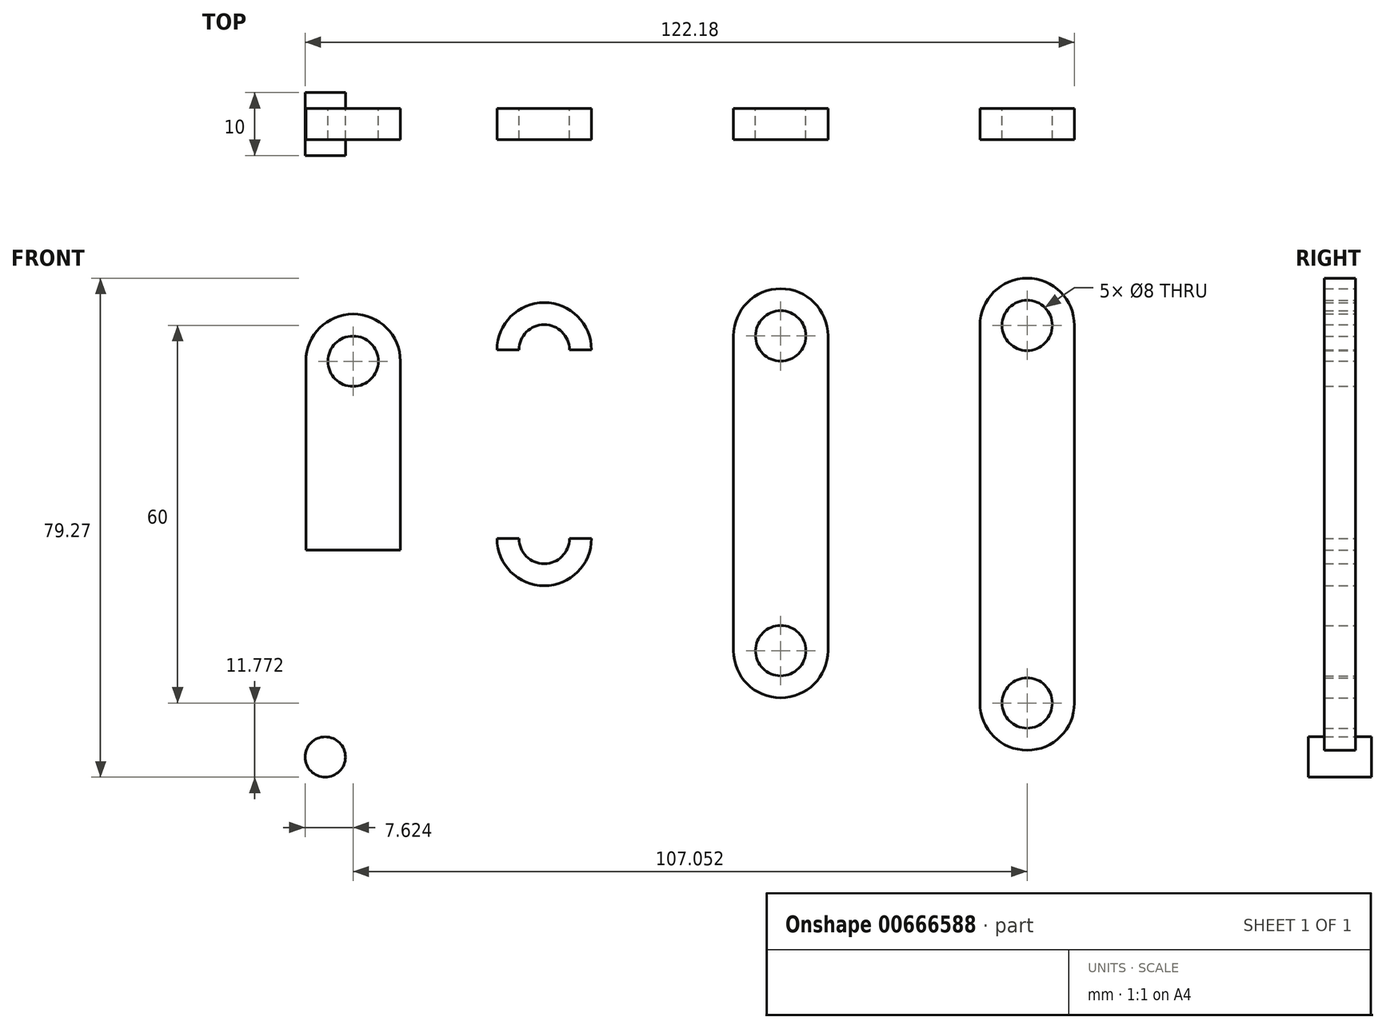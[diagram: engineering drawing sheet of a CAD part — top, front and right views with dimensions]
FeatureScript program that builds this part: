
annotation { "Feature Type Name" : "Feature", "Feature Type Description" : "" }
export const myFeature = defineFeature(function(context is Context, id is Id, definition is map)
    precondition{}
    {
        {
            var Q0;
            Q0=qCreatedBy(makeId("Front.planeOp"),FACE);
            var sketch = newSketch(context, id + "F0", { "sketchPlane" : qUnion([Q0])});
            skLineSegment(sketch, "E0.bottom", {"start": v(-59.87, 52.34) * mm, "end": v(-44.87, 52.34) * mm});
            skLineSegment(sketch, "E0.top", {"start": v(-59.87, 22.34) * mm, "end": v(-44.87, 22.34) * mm});
            skLineSegment(sketch, "E0.left", {"start": v(-59.87, 52.34) * mm, "end": v(-59.87, 22.34) * mm});
            skLineSegment(sketch, "E0.right", {"start": v(-44.87, 52.34) * mm, "end": v(-44.87, 22.34) * mm});
            skArc(sketch, "E1", {"start": v(-44.87, 52.34) * mm, "mid": v(-52.37, 59.84) * mm, "end": v(-59.87, 52.34) * mm});
            skCircle(sketch, "E2", {"center": v(-52.37, 52.34) * mm, "radius": 4 * mm});
            skSolve(sketch);
        }
        {
            var Q0;
            {var subQ0=sQuery(id+"F0.wireOp",EDGE,"E1");Q0=makeQuery(id+"F0.imprint","IMPRINT",FACE,{"disambiguationData":[TD([[makeQuery(id+"F0.imprint","IMPRINT",EDGE,{"derivedFrom":subQ0}),1.0]])]});}
            var Q1;
            Q1=makeQuery(id+"F0.imprint","IMPRINT",FACE,{"disambiguationData":[TD([[makeQuery(id+"F0.imprint","IMPRINT",EDGE,{"derivedFrom":sQuery(id+"F0.wireOp",EDGE,"E0.top")}),1.0]])]});
            extrude(context, id + "F1", {"entities" : qUnion([Q0, Q1]), "depth" : 5 * mm, "offsetDistance" : 25.4 * mm, "symmetric" : true});
        }
        {
            var Q0;
            Q0=qCreatedBy(makeId("Front.planeOp"),FACE);
            var sketch = newSketch(context, id + "F2", { "sketchPlane" : qUnion([Q0])});
            skLineSegment(sketch, "E3.bottom", {"start": v(-29.52, 54.16) * mm, "end": v(-14.52, 54.16) * mm});
            skLineSegment(sketch, "E3.top", {"start": v(-29.52, 24.16) * mm, "end": v(-14.52, 24.16) * mm});
            skLineSegment(sketch, "E3.left", {"start": v(-29.52, 54.16) * mm, "end": v(-29.52, 24.16) * mm});
            skLineSegment(sketch, "E3.right", {"start": v(-14.52, 54.16) * mm, "end": v(-14.52, 24.16) * mm});
            skArc(sketch, "E4", {"start": v(-29.52, 24.16) * mm, "mid": v(-22.02, 16.66) * mm, "end": v(-14.52, 24.16) * mm});
            skArc(sketch, "E5", {"start": v(-14.52, 54.16) * mm, "mid": v(-22.02, 61.66) * mm, "end": v(-29.52, 54.16) * mm});
            skCircle(sketch, "E6", {"center": v(-22.02, 54.16) * mm, "radius": 4 * mm});
            skCircle(sketch, "E7", {"center": v(-22.02, 24.16) * mm, "radius": 4 * mm});
            skSolve(sketch);
        }
        {
            var Q0;
            {var subQ0=sQuery(id+"F2.wireOp",EDGE,"E5");Q0=makeQuery(id+"F2.imprint","IMPRINT",FACE,{"disambiguationData":[TD([[makeQuery(id+"F2.imprint","IMPRINT",EDGE,{"derivedFrom":subQ0}),1.0]])]});}
            var Q1;
            {var subQ1=sQuery(id+"F2.wireOp",EDGE,"E3.left");Q1=makeQuery(id+"F2.imprint","IMPRINT",FACE,{"disambiguationData":[TD([[makeQuery(id+"F2.imprint","IMPRINT",EDGE,{"derivedFrom":subQ1}),1.0]])]});}
            var Q2;
            {var subQ0=sQuery(id+"F2.wireOp",EDGE,"E4");Q2=makeQuery(id+"F2.imprint","IMPRINT",FACE,{"disambiguationData":[TD([[makeQuery(id+"F2.imprint","IMPRINT",EDGE,{"derivedFrom":subQ0}),1.0]])]});}
            extrude(context, id + "F3", {"entities" : qUnion([Q0, Q1, Q2]), "depth" : 5 * mm, "offsetDistance" : 25.4 * mm, "symmetric" : true});
        }
        {
            var Q0;
            Q0=qCreatedBy(makeId("Front.planeOp"),FACE);
            var sketch = newSketch(context, id + "F4", { "sketchPlane" : qUnion([Q0])});
            skLineSegment(sketch, "E8.bottom", {"start": v(8.05, 56.36) * mm, "end": v(23.05, 56.36) * mm});
            skLineSegment(sketch, "E8.top", {"start": v(8.05, 6.36) * mm, "end": v(23.05, 6.36) * mm});
            skLineSegment(sketch, "E8.left", {"start": v(8.05, 56.36) * mm, "end": v(8.05, 6.36) * mm});
            skLineSegment(sketch, "E8.right", {"start": v(23.05, 56.36) * mm, "end": v(23.05, 6.36) * mm});
            skArc(sketch, "E9", {"start": v(23.05, 56.36) * mm, "mid": v(15.55, 63.86) * mm, "end": v(8.05, 56.36) * mm});
            skArc(sketch, "E10", {"start": v(8.05, 6.36) * mm, "mid": v(15.55, -1.14) * mm, "end": v(23.05, 6.36) * mm});
            skCircle(sketch, "E11", {"center": v(15.55, 56.36) * mm, "radius": 4 * mm});
            skCircle(sketch, "E12", {"center": v(15.55, 6.36) * mm, "radius": 4 * mm});
            skSolve(sketch);
        }
        {
            var Q0;
            Q0 = qSketchRegion(id + "F4", true);
            extrude(context, id + "F5", {"entities" : qUnion([Q0]), "depth" : 5 * mm, "offsetDistance" : 25.4 * mm, "symmetric" : true});
        }
        {
            var Q0;
            Q0=qCreatedBy(makeId("Front.planeOp"),FACE);
            var sketch = newSketch(context, id + "F6", { "sketchPlane" : qUnion([Q0])});
            skLineSegment(sketch, "E13.bottom", {"start": v(47.19, 58.03) * mm, "end": v(62.19, 58.03) * mm});
            skLineSegment(sketch, "E13.top", {"start": v(47.19, -1.97) * mm, "end": v(62.19, -1.97) * mm});
            skLineSegment(sketch, "E13.left", {"start": v(47.19, 58.03) * mm, "end": v(47.19, -1.97) * mm});
            skLineSegment(sketch, "E13.right", {"start": v(62.19, 58.03) * mm, "end": v(62.19, -1.97) * mm});
            skArc(sketch, "E14", {"start": v(47.19, -1.97) * mm, "mid": v(54.69, -9.47) * mm, "end": v(62.19, -1.97) * mm});
            skArc(sketch, "E15", {"start": v(62.19, 58.03) * mm, "mid": v(54.69, 65.53) * mm, "end": v(47.19, 58.03) * mm});
            skCircle(sketch, "E16", {"center": v(54.69, 58.03) * mm, "radius": 4 * mm});
            skCircle(sketch, "E17", {"center": v(54.69, -1.97) * mm, "radius": 4 * mm});
            skSolve(sketch);
        }
        {
            var Q0;
            Q0 = qSketchRegion(id + "F6", true);
            extrude(context, id + "F7", {"entities" : qUnion([Q0]), "depth" : 5 * mm, "offsetDistance" : 25.4 * mm, "symmetric" : true});
        }
        {
            var Q0;
            Q0=qCreatedBy(makeId("Front.planeOp"),FACE);
            var sketch = newSketch(context, id + "F8", { "sketchPlane" : qUnion([Q0])});
            skCircle(sketch, "E18", {"center": v(-56.79, -10.54) * mm, "radius": 3.2 * mm});
            skSolve(sketch);
        }
        {
            var Q0;
            Q0=makeQuery(id+"F8.imprint","IMPRINT",FACE,{"disambiguationData":[TD([[makeQuery(id+"F8.imprint","IMPRINT",EDGE,{"derivedFrom":sQuery(id+"F8.wireOp",EDGE,"E18")}),1.0]])]});
            extrude(context, id + "F9", {"entities" : qUnion([Q0]), "depth" : 10 * mm, "offsetDistance" : 25 * mm, "symmetric" : true});
        }
    });
